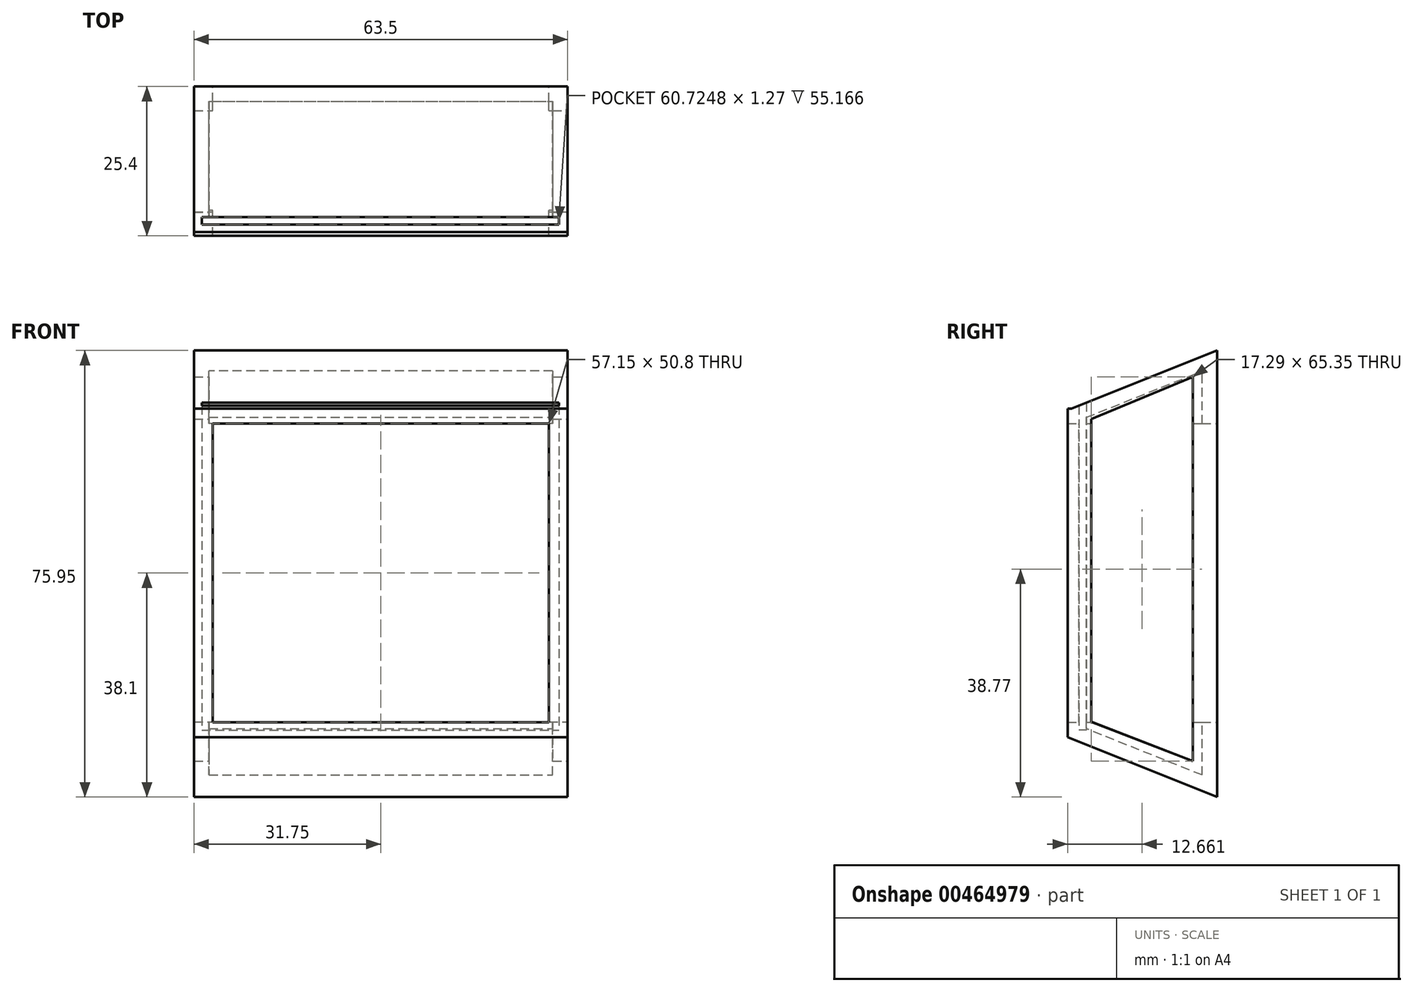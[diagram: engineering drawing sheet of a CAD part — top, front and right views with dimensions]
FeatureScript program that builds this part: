
annotation { "Feature Type Name" : "Feature", "Feature Type Description" : "" }
export const myFeature = defineFeature(function(context is Context, id is Id, definition is map)
    precondition{}
    {
        {
            var Q0;
            Q0=qCreatedBy(makeId("Front.planeOp"),FACE);
            var sketch = newSketch(context, id + "F0", { "sketchPlane" : qUnion([Q0])});
            skLineSegment(sketch, "E0.bottom", {"start": v(31.75, -38.1) * mm, "end": v(-31.75, -38.1) * mm});
            skLineSegment(sketch, "E0.top", {"start": v(31.75, 38.1) * mm, "end": v(-31.75, 38.1) * mm});
            skLineSegment(sketch, "E0.left", {"start": v(31.75, -38.1) * mm, "end": v(31.75, 38.1) * mm});
            skLineSegment(sketch, "E0.right", {"start": v(-31.75, -38.1) * mm, "end": v(-31.75, 38.1) * mm});
            skPoint(sketch, "E0.middle", {"position": v(0, 0) * mm});
            skLineSegment(sketch, "E1.bottom", {"start": v(-28.57, -25.4) * mm, "end": v(28.58, -25.4) * mm});
            skLineSegment(sketch, "E1.top", {"start": v(-28.58, 25.4) * mm, "end": v(28.57, 25.4) * mm});
            skLineSegment(sketch, "E1.left", {"start": v(-28.57, -25.4) * mm, "end": v(-28.58, 25.4) * mm});
            skLineSegment(sketch, "E1.right", {"start": v(28.58, -25.4) * mm, "end": v(28.57, 25.4) * mm});
            skSolve(sketch);
        }
        {
            var Q0;
            Q0=makeQuery(id+"F0.imprint","IMPRINT",FACE,{"disambiguationData":[TD([[makeQuery(id+"F0.imprint","IMPRINT",EDGE,{"derivedFrom":sQuery(id+"F0.wireOp",EDGE,"E0.bottom")}),-1.0]])]});
            extrude(context, id + "F1", {"entities" : qUnion([Q0]), "depth" : 25.4 * mm});
        }
        {
            var Q0;
            Q0=makeQuery(id+"F1.opExtrude","CAP_EDGE",EDGE,{"disambiguationData":[OSD([sQuery(id+"F0.wireOp",EDGE,"E0.top")])],"isStart":false});
            var Q1;
            Q1=makeQuery(id+"F1.opExtrude","CAP_EDGE",EDGE,{"disambiguationData":[OSD([sQuery(id+"F0.wireOp",EDGE,"E0.bottom")])],"isStart":false});
            chamfer(context, id + "F2", {"entities" : qUnion([Q0, Q1]), "chamferType" : ChamferType.TWO_OFFSETS, "width1" : 10.16 * mm, "oppositeDirection" : false, "width2" : 25.4 * mm, "tangentPropagation" : true});
        }
        {
            var Q0;
            Q0=makeQuery(id+"F1.opExtrude","SWEPT_FACE",FACE,{"disambiguationData":[OSD([sQuery(id+"F0.wireOp",EDGE,"E1.bottom")])]});
            var Q1;
            Q1=makeQuery(id+"F1.opExtrude","SWEPT_FACE",FACE,{"disambiguationData":[OSD([sQuery(id+"F0.wireOp",EDGE,"E1.top")])]});
            shell(context, id + "F3", {"entities" : qUnion([Q0, Q1]), "thickness" : 2.54 * mm});
        }
        {
            var Q0;
            Q0=qCreatedBy(makeId("Front.planeOp"),FACE);
            var sketch = newSketch(context, id + "F4", { "sketchPlane" : qUnion([Q0])});
            skLineSegment(sketch, "E2.bottom", {"start": v(-41.94, 53.8) * mm, "end": v(42.73, 53.8) * mm});
            skLineSegment(sketch, "E2.top", {"start": v(-41.94, -57.37) * mm, "end": v(42.73, -57.37) * mm});
            skLineSegment(sketch, "E2.left", {"start": v(-41.94, 53.8) * mm, "end": v(-41.94, -57.37) * mm});
            skLineSegment(sketch, "E2.right", {"start": v(42.73, 53.8) * mm, "end": v(42.73, -57.37) * mm});
            skSolve(sketch);
        }
        {
            var Q0;
            Q0=makeQuery(id+"F4.imprint","IMPRINT",FACE,{"disambiguationData":[TD([[makeQuery(id+"F4.imprint","IMPRINT",EDGE,{"derivedFrom":sQuery(id+"F4.wireOp",EDGE,"E2.bottom")}),-1.0]])]});
            cPlane(context, id + "F5", {"entities" : qUnion([Q0]), "cplaneType" : CPlaneType.OFFSET, "offset" : 22.86 * mm, "width" : 152.4 * mm, "height" : 152.4 * mm});
        }
        {
            var Q0;
            Q0=qCreatedBy(id+"F5.planeOp",FACE);
            var sketch = newSketch(context, id + "F6", { "sketchPlane" : qUnion([Q0])});
            skLineSegment(sketch, "E3.bottom", {"start": v(-30.43, 40.03) * mm, "end": v(30.3, 40.03) * mm});
            skLineSegment(sketch, "E3.top", {"start": v(-30.43, -26.72) * mm, "end": v(30.3, -26.72) * mm});
            skLineSegment(sketch, "E3.left", {"start": v(-30.43, 40.03) * mm, "end": v(-30.43, -26.72) * mm});
            skLineSegment(sketch, "E3.right", {"start": v(30.3, 40.03) * mm, "end": v(30.3, -26.72) * mm});
            skSolve(sketch);
        }
        {
            var Q0;
            Q0=makeQuery(id+"F6.imprint","IMPRINT",FACE,{"disambiguationData":[TD([[makeQuery(id+"F6.imprint","IMPRINT",EDGE,{"derivedFrom":sQuery(id+"F6.wireOp",EDGE,"E3.bottom")}),-1.0]])]});
            var Q1;
            Q1=makeQuery(id+"F2.opChamfer","BLEND_FACE",FACE,{"disambiguationData":[OSD([sQuery(id+"F0.wireOp",EDGE,"E0.top")])]});
            extrude(context, id + "F7", {"entities" : qUnion([Q0, Q1]), "operationType" : NewBodyOperationType.REMOVE, "oppositeDirection" : true, "depth" : 1.27 * mm, "symmetric" : true});
        }
        {
            var Q0;
            Q0=qCreatedBy(makeId("Right.planeOp"),FACE);
            var sketch = newSketch(context, id + "F8", { "sketchPlane" : qUnion([Q0])});
            skLineSegment(sketch, "E4", {"start": v(-21.38, 26.18) * mm, "end": v(-4.1, 33.35) * mm});
            skLineSegment(sketch, "E5", {"start": v(-4.1, 33.35) * mm, "end": v(-4.1, -32) * mm});
            skLineSegment(sketch, "E6", {"start": v(-4.1, -32) * mm, "end": v(-21.35, -25.3) * mm});
            skLineSegment(sketch, "E7", {"start": v(-21.35, -25.3) * mm, "end": v(-21.38, 26.18) * mm});
            skSolve(sketch);
        }
        {
            var Q0;
            Q0=makeQuery(id+"F8.imprint","IMPRINT",FACE,{"disambiguationData":[TD([[makeQuery(id+"F8.imprint","IMPRINT",EDGE,{"derivedFrom":sQuery(id+"F8.wireOp",EDGE,"E4")}),-1.0]])]});
            extrude(context, id + "F9", {"entities" : qUnion([Q0]), "operationType" : NewBodyOperationType.REMOVE, "oppositeDirection" : true, "depth" : 88.9 * mm, "symmetric" : true});
        }
    });
